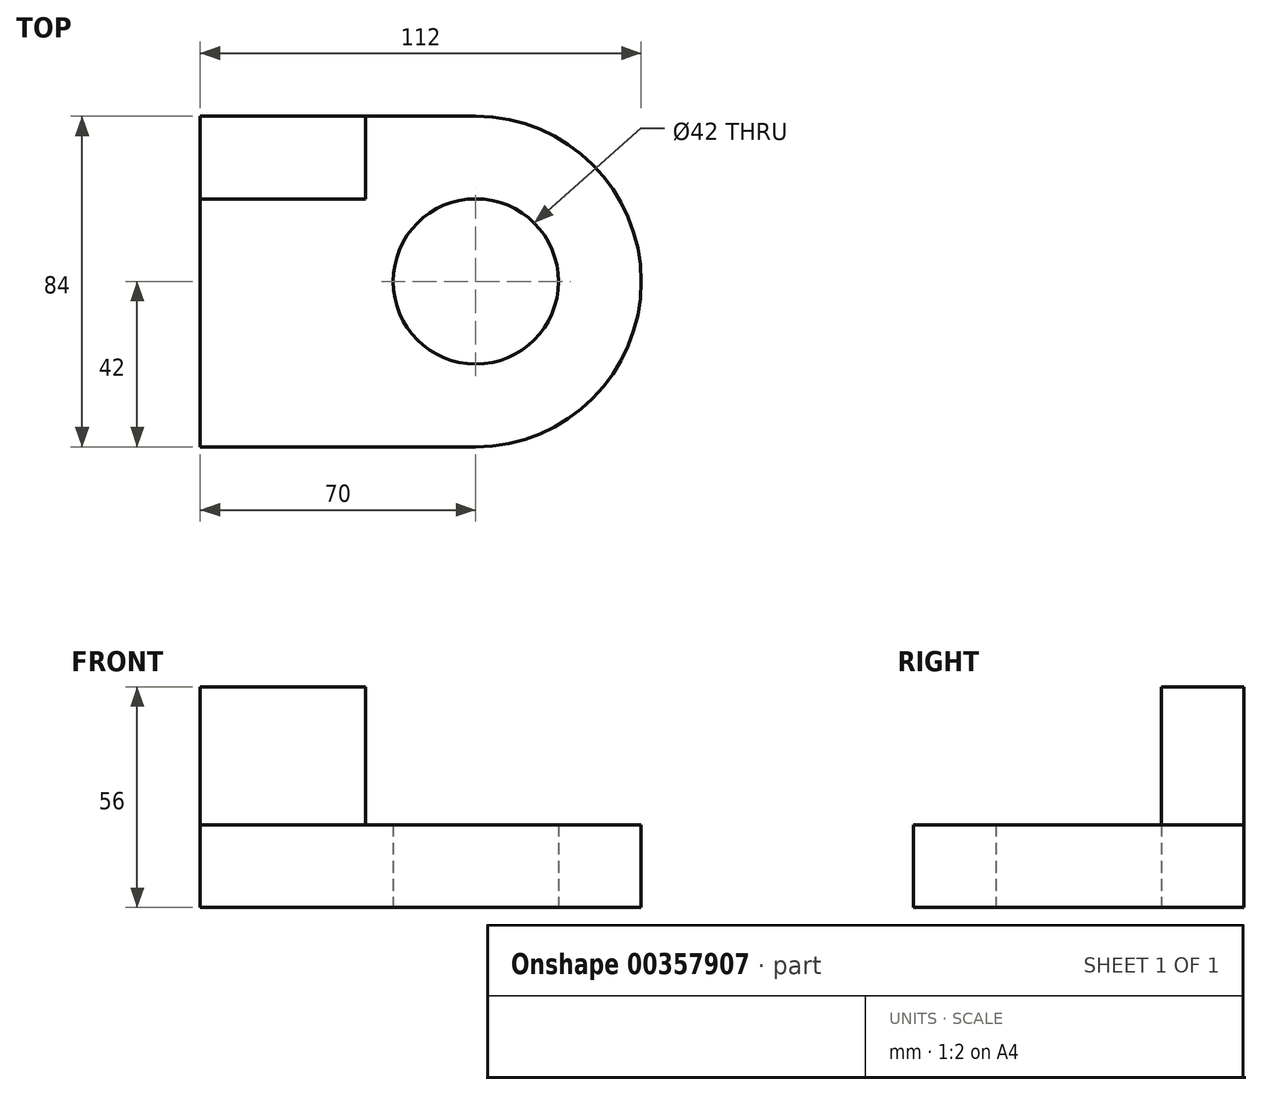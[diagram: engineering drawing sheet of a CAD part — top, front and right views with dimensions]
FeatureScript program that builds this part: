
annotation { "Feature Type Name" : "Feature", "Feature Type Description" : "" }
export const myFeature = defineFeature(function(context is Context, id is Id, definition is map)
    precondition{}
    {
        {
            var Q0;
            Q0=qCreatedBy(makeId("Top.planeOp"),FACE);
            var sketch = newSketch(context, id + "F0", { "sketchPlane" : qUnion([Q0])});
            skLineSegment(sketch, "E0.bottom", {"start": v(-56, 42) * mm, "end": v(14, 42) * mm});
            skLineSegment(sketch, "E0.top", {"start": v(-56, -42) * mm, "end": v(14, -42) * mm});
            skLineSegment(sketch, "E0.left", {"start": v(-56, 42) * mm, "end": v(-56, -42) * mm});
            skLineSegment(sketch, "E0.right", {"start": v(56, 0) * mm, "end": v(56, -42) * mm});
            skPoint(sketch, "E0.middle", {"position": v(0, 0) * mm});
            skCircle(sketch, "E1", {"center": v(14, 0) * mm, "radius": 21 * mm});
            skArc(sketch, "E2", {"start": v(14, -42) * mm, "mid": v(56, 0) * mm, "end": v(14, 42) * mm});
            skPoint(sketch, "E3.orphan", {"position": v(56, 42) * mm});
            skSolve(sketch);
        }
        {
            var Q0;
            Q0 = qSketchRegion(id + "F0", true);
            extrude(context, id + "F1", {"entities" : qUnion([Q0]), "depth" : 21 * mm});
        }
        {
            var Q0;
            Q0=makeQuery(id+"F1.opExtrude","CAP_FACE",FACE,{"disambiguationData":[OSD([sQuery(id+"F0.wireOp",EDGE,"E0.bottom"),sQuery(id+"F0.wireOp",EDGE,"E0.top"),sQuery(id+"F0.wireOp",EDGE,"E0.left"),sQuery(id+"F0.wireOp",EDGE,"E1"),sQuery(id+"F0.wireOp",EDGE,"E2")])],"isStart":false});
            var sketch = newSketch(context, id + "F2", { "sketchPlane" : qUnion([Q0])});
            skLineSegment(sketch, "E4.bottom", {"start": v(-56, 42) * mm, "end": v(-14, 42) * mm});
            skLineSegment(sketch, "E4.top", {"start": v(-56, 21) * mm, "end": v(-14, 21) * mm});
            skLineSegment(sketch, "E4.left", {"start": v(-56, 42) * mm, "end": v(-56, 21) * mm});
            skLineSegment(sketch, "E4.right", {"start": v(-14, 42) * mm, "end": v(-14, 21) * mm});
            skSolve(sketch);
        }
        {
            var Q0;
            Q0 = qSketchRegion(id + "F2", true);
            extrude(context, id + "F3", {"entities" : qUnion([Q0]), "operationType" : NewBodyOperationType.ADD, "depth" : 35 * mm});
        }
    });
